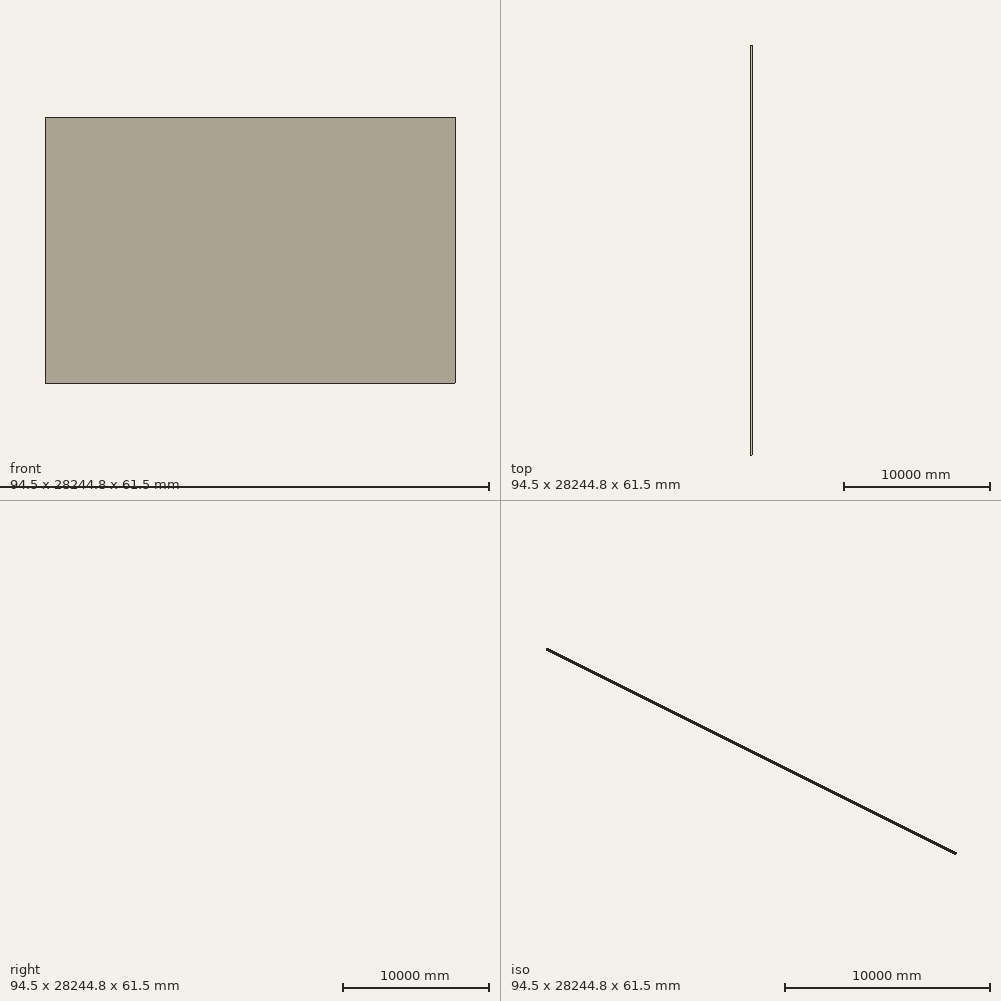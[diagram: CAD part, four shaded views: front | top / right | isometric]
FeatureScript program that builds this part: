
annotation { "Feature Type Name" : "Feature", "Feature Type Description" : "" }
export const myFeature = defineFeature(function(context is Context, id is Id, definition is map)
    precondition{}
    {
        {
            var Q0;
            Q0=qCreatedBy(makeId("Front.planeOp"),FACE);
            var sketch = newSketch(context, id + "F0", { "sketchPlane" : qUnion([Q0])});
            skLineSegment(sketch, "E0.bottom", {"start": v(-46.81, 34.44) * mm, "end": v(47.64, 34.44) * mm});
            skLineSegment(sketch, "E0.top", {"start": v(-46.81, -27.01) * mm, "end": v(47.64, -27.01) * mm});
            skLineSegment(sketch, "E0.left", {"start": v(-46.81, 34.44) * mm, "end": v(-46.81, -27.01) * mm});
            skLineSegment(sketch, "E0.right", {"start": v(47.64, 34.44) * mm, "end": v(47.64, -27.01) * mm});
            skSolve(sketch);
        }
        {
            var Q0;
            Q0=makeQuery(id+"F0.imprint","IMPRINT",FACE,{"disambiguationData":[TD([[makeQuery(id+"F0.imprint","IMPRINT",EDGE,{"derivedFrom":sQuery(id+"F0.wireOp",EDGE,"E0.bottom")}),-1.0]])]});
            extrude(context, id + "F1", {"entities" : qUnion([Q0]), "depth" : 25.4 * mm, "offsetDistance" : 25.4 * mm});
        }
        {
            var Q0;
            Q0=makeQuery(id+"F0.imprint","IMPRINT",FACE,{"disambiguationData":[TD([[makeQuery(id+"F0.imprint","IMPRINT",EDGE,{"derivedFrom":sQuery(id+"F0.wireOp",EDGE,"E0.bottom")}),-1.0]])]});
            extrude(context, id + "F2", {"entities" : qUnion([Q0]), "operationType" : NewBodyOperationType.ADD, "depth" : -28219.4 * mm, "offsetDistance" : 25.4 * mm});
        }
    });
